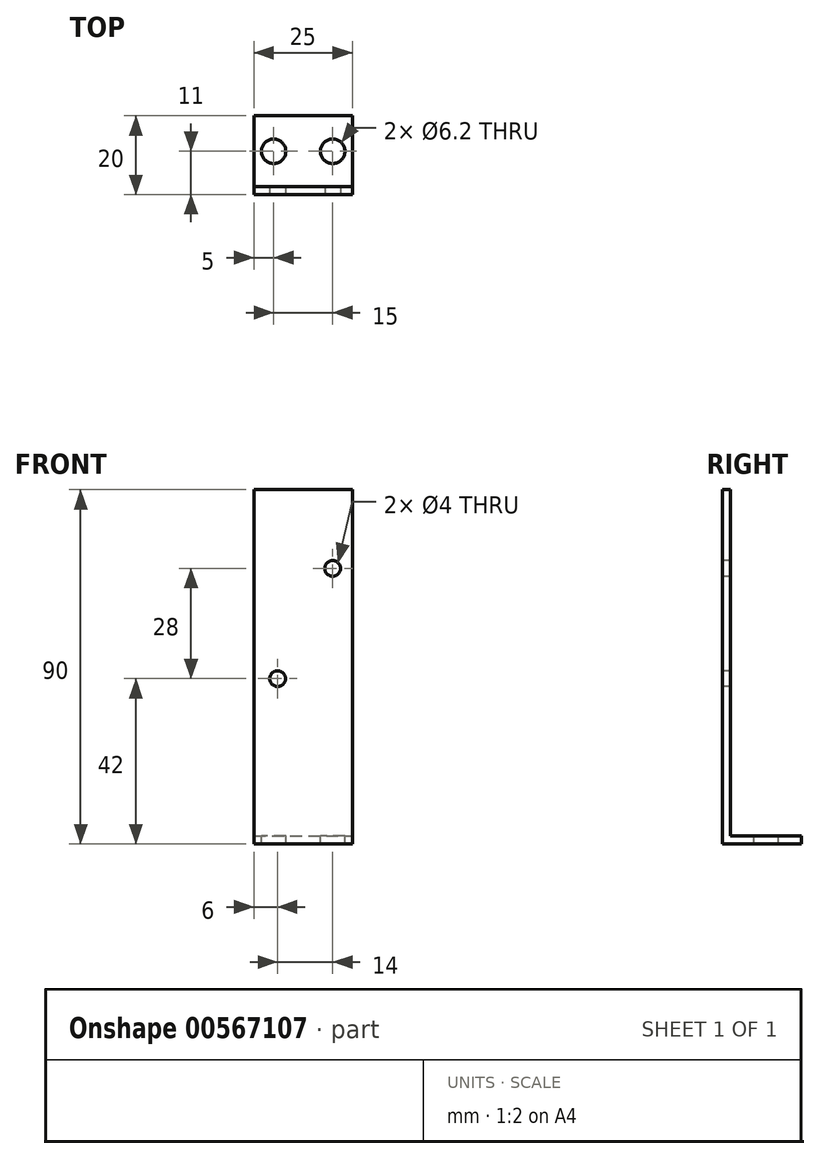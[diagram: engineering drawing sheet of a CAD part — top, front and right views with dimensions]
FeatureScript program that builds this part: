
annotation { "Feature Type Name" : "Feature", "Feature Type Description" : "" }
export const myFeature = defineFeature(function(context is Context, id is Id, definition is map)
    precondition{}
    {
        {
            var Q0;
            Q0=qCreatedBy(makeId("Front.planeOp"),FACE);
            var sketch = newSketch(context, id + "F0", { "sketchPlane" : qUnion([Q0])});
            skLineSegment(sketch, "E0.bottom", {"start": v(-12.5, 45) * mm, "end": v(12.5, 45) * mm});
            skLineSegment(sketch, "E0.top", {"start": v(-12.5, -45) * mm, "end": v(12.5, -45) * mm});
            skLineSegment(sketch, "E0.left", {"start": v(-12.5, 45) * mm, "end": v(-12.5, -45) * mm});
            skLineSegment(sketch, "E0.right", {"start": v(12.5, 45) * mm, "end": v(12.5, -45) * mm});
            skPoint(sketch, "E0.middle", {"position": v(0, 0) * mm});
            skSolve(sketch);
        }
        {
            var Q0;
            Q0=makeQuery(id+"F0.imprint","IMPRINT",FACE,{"disambiguationData":[TD([[makeQuery(id+"F0.imprint","IMPRINT",EDGE,{"derivedFrom":sQuery(id+"F0.wireOp",EDGE,"E0.bottom")}),-1.0]])]});
            extrude(context, id + "F1", {"entities" : qUnion([Q0]), "depth" : 2 * mm, "offsetDistance" : 25 * mm});
        }
        {
            var Q0;
            Q0=makeQuery(id+"F1.opExtrude","CAP_FACE",FACE,{"disambiguationData":[OSD([sQuery(id+"F0.wireOp",EDGE,"E0.bottom"),sQuery(id+"F0.wireOp",EDGE,"E0.top"),sQuery(id+"F0.wireOp",EDGE,"E0.left"),sQuery(id+"F0.wireOp",EDGE,"E0.right")])],"isStart":false});
            var sketch = newSketch(context, id + "F2", { "sketchPlane" : qUnion([Q0])});
            skLineSegment(sketch, "E1.bottom", {"start": v(-12.5, -45) * mm, "end": v(12.5, -45) * mm});
            skLineSegment(sketch, "E1.top", {"start": v(-12.5, -43) * mm, "end": v(12.5, -43) * mm});
            skLineSegment(sketch, "E1.left", {"start": v(-12.5, -45) * mm, "end": v(-12.5, -43) * mm});
            skLineSegment(sketch, "E1.right", {"start": v(12.5, -45) * mm, "end": v(12.5, -43) * mm});
            skSolve(sketch);
        }
        {
            var Q0;
            Q0=makeQuery(id+"F2.imprint","IMPRINT",FACE,{"disambiguationData":[TD([[makeQuery(id+"F2.imprint","IMPRINT",EDGE,{"derivedFrom":sQuery(id+"F2.wireOp",EDGE,"E1.bottom")}),1.0]])]});
            extrude(context, id + "F3", {"entities" : qUnion([Q0]), "operationType" : NewBodyOperationType.ADD, "oppositeDirection" : true, "depth" : 20 * mm, "offsetDistance" : 25 * mm});
        }
        {
            var Q0;
            Q0=makeQuery(id+"F1.opExtrude","CAP_FACE",FACE,{"disambiguationData":[OSD([sQuery(id+"F0.wireOp",EDGE,"E0.bottom"),sQuery(id+"F0.wireOp",EDGE,"E0.top"),sQuery(id+"F0.wireOp",EDGE,"E0.left"),sQuery(id+"F0.wireOp",EDGE,"E0.right")])],"isStart":false});
            var sketch = newSketch(context, id + "F4", { "sketchPlane" : qUnion([Q0])});
            skCircle(sketch, "E2", {"center": v(7.5, 25) * mm, "radius": 2 * mm});
            skCircle(sketch, "E3", {"center": v(-6.5, -3) * mm, "radius": 2 * mm});
            skSolve(sketch);
        }
        {
            var Q0;
            Q0 = qSketchRegion(id + "F4", true);
            extrude(context, id + "F5", {"entities" : qUnion([Q0]), "operationType" : NewBodyOperationType.REMOVE, "oppositeDirection" : true, "depth" : 25 * mm, "offsetDistance" : 25 * mm});
        }
        {
            var Q0;
            Q0=makeQuery(id+"F3.opExtrude","SWEPT_FACE",FACE,{"disambiguationData":[OSD([sQuery(id+"F2.wireOp",EDGE,"E1.top")])]});
            var sketch = newSketch(context, id + "F6", { "sketchPlane" : qUnion([Q0])});
            skCircle(sketch, "E4", {"center": v(7.5, 9) * mm, "radius": 3.1 * mm});
            skPoint(sketch, "E4.centerSnap0", {"position": v(12.5, 9) * mm});
            skCircle(sketch, "E5", {"center": v(-7.5, 9) * mm, "radius": 3.1 * mm});
            skPoint(sketch, "E5.centerSnap0", {"position": v(4.65, 9) * mm});
            skSolve(sketch);
        }
        {
            var Q0;
            Q0 = qSketchRegion(id + "F6", true);
            extrude(context, id + "F7", {"entities" : qUnion([Q0]), "operationType" : NewBodyOperationType.REMOVE, "oppositeDirection" : true, "depth" : 25 * mm, "offsetDistance" : 25 * mm});
        }
    });
